# Revit family: Lighting_Outside_Focus-Lighting_Way-top-entry(Recovery)
name_source: partatom
category: Lighting Fixtures
revit_build: Autodesk Revit 2015 (Build: 20140903_1530(x64)
units: mm (PartAtom-declared; Revit-internal decimal feet)

## types (1)
- 9801-9830
    BIMobject category = Outside
    BIMobject category code = lighting-outside
    BIMobject main category = Lighting
    BIMobject main category code = lighting
    BOSUseNativeGeometries = 1
    Brand url = http://focus-lighting.dk
    Classification = IP66 class II
    Color Filter = 16777215
    Colour = Silver grey MW300D AB71E298
    Colour accuracy = 4 steps SDCM
    Colour rendering = min 70  typically 75 Ra option for 80 Ra
    Connection = In the post; Delivered with lead; either 2 off 2 m 2.5 mm2 or 1 off 10 m 2 x 1 mm2
    Design country = Denmark
    Dimming = 8-100% programming range
    Dimming Lamp Color Temperature Shift = <None>
    Driver = Xitanium Full Xi FP 75 W 0.2-0.7 A programmable
    Driver Operational life = min 100.000 hours
    Edition number = 1
    IFC Classification = Lamp
    Impact resistance = IK10
    Inrush current = max 46 A (50% after 250 µs)
    LED Operational life = min 100.000 hours at ta max 25° C L80B10
    LED circular = Ø240 64 diodes CAT lenses
    Luminous power = 3000K: min 2240 max 9000 lm CLO
    Manufacturer country = Denmark
    Manufacturer name = Focus Lighting
    Masterformat 2014 Code = 12 43 13
    Masterformat 2014 Description = Lamps
    Material = Cast aluminium
    Material main = Aluminium
    Material secondary = Polycarbonate
    Max pre-protection = 16 A
    Mounting = 3/4 threaded tube
    NBS Reference Code = 49
    NBS Reference Description = Luminaires And Lamps
    Nominal frequency range = 50-60 Hz
    Nominal height = 276
    Nominal voltage AC = 220-240 Vac
    Nominal width = 480
    Nominel voltage DC = 186-250 Vdc
    OmniClass Code = 23-35 45 15
    OmniClass Description = Lamps
    Operational frequency range = 45-66 Hz
    Operational input voltage AC = 150-264 Vac
    Operational input voltage DC = 165-275 Vdc
    Photometric Web File = generic
    Product Guid = 68692e95-589a-437c-a147-e9d81b45ac80
    Product SKU = way-top-entry
    Product data url = https://bimobject.com
    Product family = Outdoor
    Product group = Catenary
    Product name = Way top entry
    Product url = http://www.focus-lighting.dk
    QR code = http://bimobject.com
    Shade = Clear impact resistance PMMA with frosted edge
    Surge protection = L/N-GND: 8 kV; L-N: 6 kV
    Technical description = http://www.focus-lighting.dk
    Temperature range = -30 to +35° C
    Tilt Angle = 90.00°
    UNSPSC Code = 391016
    Uniclass 1.4 Code = L7474
    Uniclass 1.4 Description = Lamps
    Uniclass 2.0 Code = PR-49
    Uniclass 2.0 Description = Luminaires And Lamps
    Uniclass 2015 Code = Pr_70_70_46
    Uniclass 2015 Name = Lamps
    Weight = ca 10 kg
    Weight Net (Kg) = 10

## geometry (parser evidence)
native form markers: Sweep x3
no freeform markers — native parametric forms only
